# Revit family: Haworth_Masters_Desk_CredenzawithPedestals
name_source: partatom
category: Furniture Systems
revit_build: Autodesk Revit 2018 (Build: 20170223_1515(x64)
units: mm (PartAtom-declared; Revit-internal decimal feet)

## family parameters
Always vertical = Yes
Cut with Voids When Loaded = No
OmniClass Number = 23.40.70.14.64.21
OmniClass Title = Systems Furniture
Part Type = Normal
Room Calculation Point = No
Round Connector Dimension = Use Diameter
Shared = No
Work Plane-Based = No

## types (1)
- XZZP-2472
    Actual Depth = 24"
    Actual Height = 29 1/8"
    Actual Width = 72"
    Assembly Code = E2020200
    Bar Pull = Yes
    Classic Pull = No
    Description = Haworth - Masters Desk - Credenza with Pedestals
    Finger Pull = No
    Linear Pull = No
    Manufacturer = Haworth
    Model = XZZP
    Pedestal Depth = 23"
    Revision Number = 1
    Size = Verify Final Dim. w/ Haworth
    Sustainability Info = https://www.haworth.com
    Thickness = 1 3/16"
    URL = www.haworth.com
    URL - Product = http://www.haworth.com
    Warranty = http://www.haworth.com
    With Grommet = Yes

## geometry (parser evidence)
native form markers: Sweep x11
no freeform markers — native parametric forms only
